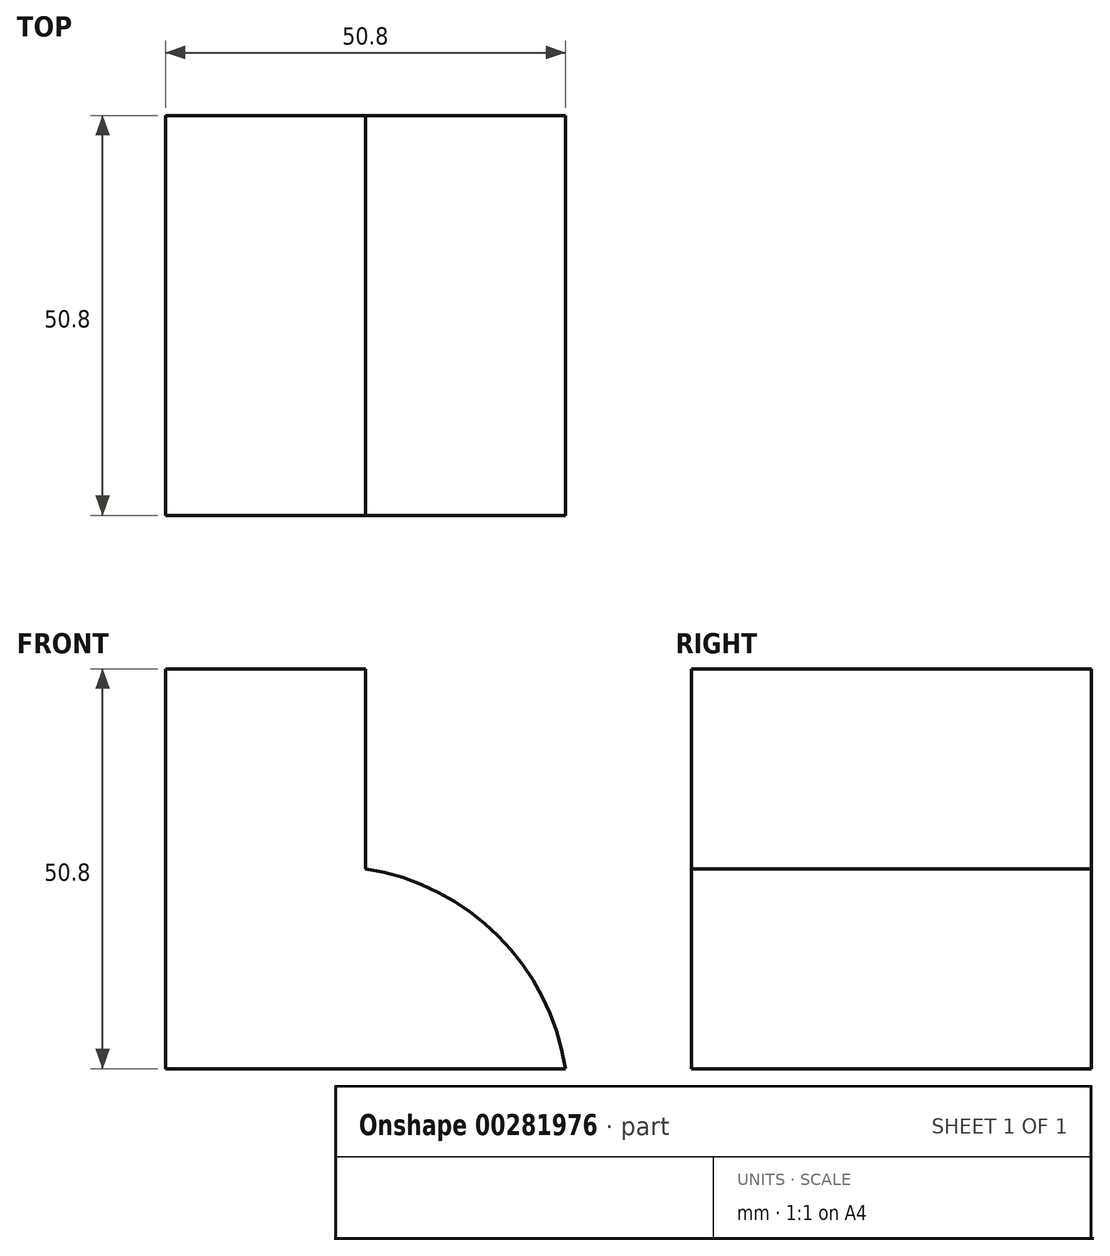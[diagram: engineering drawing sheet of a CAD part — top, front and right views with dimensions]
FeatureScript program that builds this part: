
annotation { "Feature Type Name" : "Feature", "Feature Type Description" : "" }
export const myFeature = defineFeature(function(context is Context, id is Id, definition is map)
    precondition{}
    {
        {
            var Q0;
            Q0=qCreatedBy(makeId("Front.planeOp"),FACE);
            var sketch = newSketch(context, id + "F0", { "sketchPlane" : qUnion([Q0])});
            skLineSegment(sketch, "E0", {"start": v(-54.61, 75.43) * mm, "end": v(-54.61, 24.63) * mm});
            skLineSegment(sketch, "E1", {"start": v(-54.61, 24.63) * mm, "end": v(-3.81, 24.63) * mm});
            skLineSegment(sketch, "E2", {"start": v(-3.81, 24.63) * mm, "end": v(-54.61, 24.63) * mm});
            skLineSegment(sketch, "E3", {"start": v(-54.61, 75.43) * mm, "end": v(-29.21, 75.43) * mm});
            skLineSegment(sketch, "E4", {"start": v(-29.21, 75.43) * mm, "end": v(-29.21, 50.03) * mm});
            skArc(sketch, "E5", {"start": v(-3.81, 24.63) * mm, "mid": v(-12.36, 41.48) * mm, "end": v(-29.21, 50.03) * mm});
            skSolve(sketch);
        }
        {
            var Q0;
            Q0 = qSketchRegion(id + "F0", true);
            extrude(context, id + "F1", {"entities" : qUnion([Q0]), "depth" : 50.8 * mm});
        }
    });
